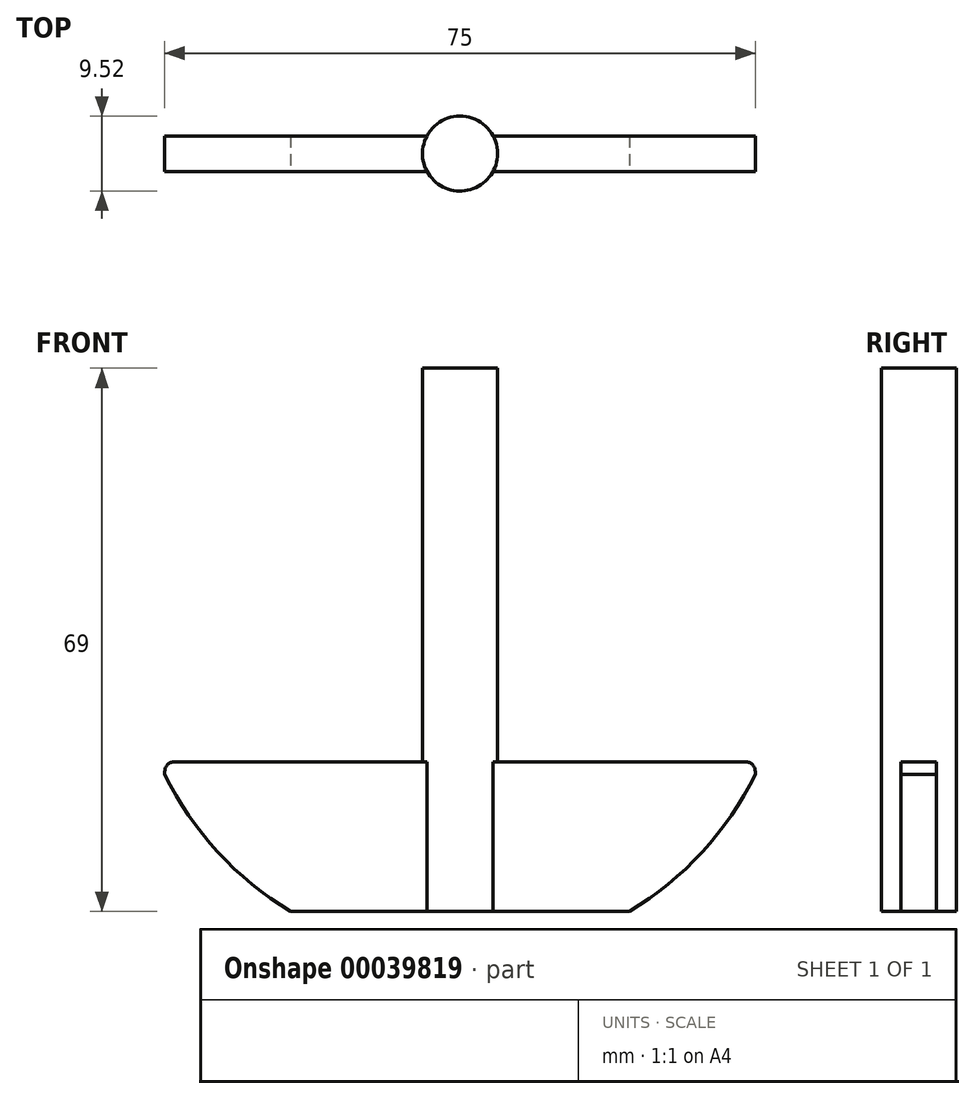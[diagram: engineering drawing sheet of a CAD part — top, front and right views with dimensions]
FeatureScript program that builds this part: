
annotation { "Feature Type Name" : "Feature", "Feature Type Description" : "" }
export const myFeature = defineFeature(function(context is Context, id is Id, definition is map)
    precondition{}
    {
        {
            var Q0;
            Q0=qCreatedBy(makeId("Top.planeOp"),FACE);
            var sketch = newSketch(context, id + "F0", { "sketchPlane" : qUnion([Q0])});
            skLineSegment(sketch, "E0.bottom", {"start": v(-7.96, 2) * mm, "end": v(25.34, 2) * mm});
            skLineSegment(sketch, "E0.top", {"start": v(-7.96, -2.5) * mm, "end": v(25.34, -2.5) * mm});
            skLineSegment(sketch, "E0.left", {"start": v(-7.96, 2) * mm, "end": v(-7.96, -2.5) * mm});
            skLineSegment(sketch, "E0.right", {"start": v(67.04, 2) * mm, "end": v(67.04, -2.5) * mm});
            skLineSegment(sketch, "E1", {"start": v(29.54, 2) * mm, "end": v(29.54, -16.68) * mm, "construction": true});
            skLineSegment(sketch, "E2", {"start": v(-7.96, -0.24) * mm, "end": v(37.53, -0.24) * mm, "construction": true});
            skArc(sketch, "E3", {"start": v(25.34, -2.5) * mm, "mid": v(29.54, -5) * mm, "end": v(33.73, -2.5) * mm});
            skArc(sketch, "E4.trimOffspring", {"start": v(33.73, 2) * mm, "mid": v(29.54, 4.52) * mm, "end": v(25.34, 2) * mm});
            skLineSegment(sketch, "E5.trimOffspring", {"start": v(33.73, 2) * mm, "end": v(67.04, 2) * mm});
            skLineSegment(sketch, "E6.trimOffspring", {"start": v(33.73, -2.5) * mm, "end": v(67.04, -2.5) * mm});
            skSolve(sketch);
        }
        {
            var Q0;
            Q0=qSketchRegion(id+"F0",true);
            extrude(context, id + "F1", {"entities" : qUnion([Q0]), "depth" : 19 * mm});
        }
        {
            var Q0;
            Q0=makeQuery(id+"F1.opExtrude","CAP_FACE",FACE,{"disambiguationData":[OSD([sQuery(id+"F0.wireOp",EDGE,"E0.bottom"),sQuery(id+"F0.wireOp",EDGE,"E0.top"),sQuery(id+"F0.wireOp",EDGE,"E0.left"),sQuery(id+"F0.wireOp",EDGE,"E0.right"),sQuery(id+"F0.wireOp",EDGE,"E3"),sQuery(id+"F0.wireOp",EDGE,"E4.trimOffspring"),sQuery(id+"F0.wireOp",EDGE,"E5.trimOffspring"),sQuery(id+"F0.wireOp",EDGE,"E6.trimOffspring")])],"isStart":false});
            var sketch = newSketch(context, id + "F2", { "sketchPlane" : qUnion([Q0])});
            skCircle(sketch, "E7", {"center": v(29.54, -0.24) * mm, "radius": 4.76 * mm});
            skSolve(sketch);
        }
        {
            var Q0;
            Q0=qSketchRegion(id+"F2",true);
            extrude(context, id + "F3", {"entities" : qUnion([Q0]), "operationType" : NewBodyOperationType.ADD, "depth" : 50 * mm});
        }
        {
            var Q0;
            Q0=makeQuery(id+"F1.opExtrude","SWEPT_FACE",FACE,{"disambiguationData":[OSD([sQuery(id+"F0.wireOp",EDGE,"E0.top")])]});
            var sketch = newSketch(context, id + "F4", { "sketchPlane" : qUnion([Q0])});
            skArc(sketch, "E8", {"start": v(-9.13, 19.99) * mm, "mid": v(-2.18, 8.6) * mm, "end": v(8, 0) * mm});
            skLineSegment(sketch, "E9", {"start": v(8, 0) * mm, "end": v(51.07, 0) * mm});
            skArc(sketch, "E10.trimOffspring", {"start": v(51.07, 0) * mm, "mid": v(61.3, 8.67) * mm, "end": v(68.27, 20.14) * mm});
            skLineSegment(sketch, "E11", {"start": v(8, 0) * mm, "end": v(-9.13, 0) * mm});
            skLineSegment(sketch, "E12", {"start": v(-9.13, 0) * mm, "end": v(-9.13, 19.99) * mm});
            skLineSegment(sketch, "E13", {"start": v(51.07, 0) * mm, "end": v(68.75, 0) * mm});
            skLineSegment(sketch, "E14", {"start": v(68.75, 0) * mm, "end": v(68.27, 20.14) * mm});
            skSolve(sketch);
        }
        {
            var Q0;
            Q0=qSketchRegion(id+"F4",true);
            extrude(context, id + "F5", {"entities" : qUnion([Q0]), "operationType" : NewBodyOperationType.REMOVE, "endBound" : BoundingType.THROUGH_ALL, "oppositeDirection" : true, "depth" : 25 * mm});
        }
        {
            var Q0;
            Q0=makeQuery(id+"F1.opExtrude","CAP_EDGE",EDGE,{"disambiguationData":[OSD([sQuery(id+"F0.wireOp",EDGE,"E0.right")])],"isStart":false});
            var Q1;
            Q1=makeQuery(id+"F1.opExtrude","CAP_EDGE",EDGE,{"disambiguationData":[OSD([sQuery(id+"F0.wireOp",EDGE,"E0.left")])],"isStart":false});
            fillet(context, id + "F6", {"entities" : qUnion([Q0, Q1]), "radius" : 1.2 * mm, "tangentPropagation" : true, "allowEdgeOverflow" : false});
        }
    });
